# Revit family: S4R_OBO BETTERMANN_CableTray_Vertical_Bracket
name_source: partatom
category: Cable Tray Fittings
revit_build: Autodesk Revit MEP 2012 (Build: 20110309_2315(x64)
units: mm (PartAtom-declared; Revit-internal decimal feet)

## types (1)
- BF 140 10 FT
    ARTICLEDESCRIPTION = Cable Tray Vertical Bracket
    ARTICLENUMBER = 6356362
    BodyColor = Steel
    DEEPLINK = http://catalog1.obo-bettermann.com
    Depth = 40 mm  [stored 0.131234 ft]
    Description = Cable Tray Vertical Bracket
    GTINNUMBER = 4012196295876
    HEIGHT = 119 mm
    HEIGHT1 = 119 mm  [stored 0.39042 ft]
    Manufacturer = OBO BETTERMANN
    PRODUCTLINE = OBO BETTERMANN CableTrays
    TYPE = BF 140 10 FT
    URL = www.stabiplan.com
    VERSION = 91900
    WIDTH = 110 mm
    WIDTH1 = 110 mm  [stored 0.360892 ft]

note: [stored X ft] marks values corroborated as IEEE doubles in the binary element streams (Revit-internal decimal feet)

## geometry (parser evidence)
native form markers: Blend x4, Sweep x2
no freeform markers — native parametric forms only
